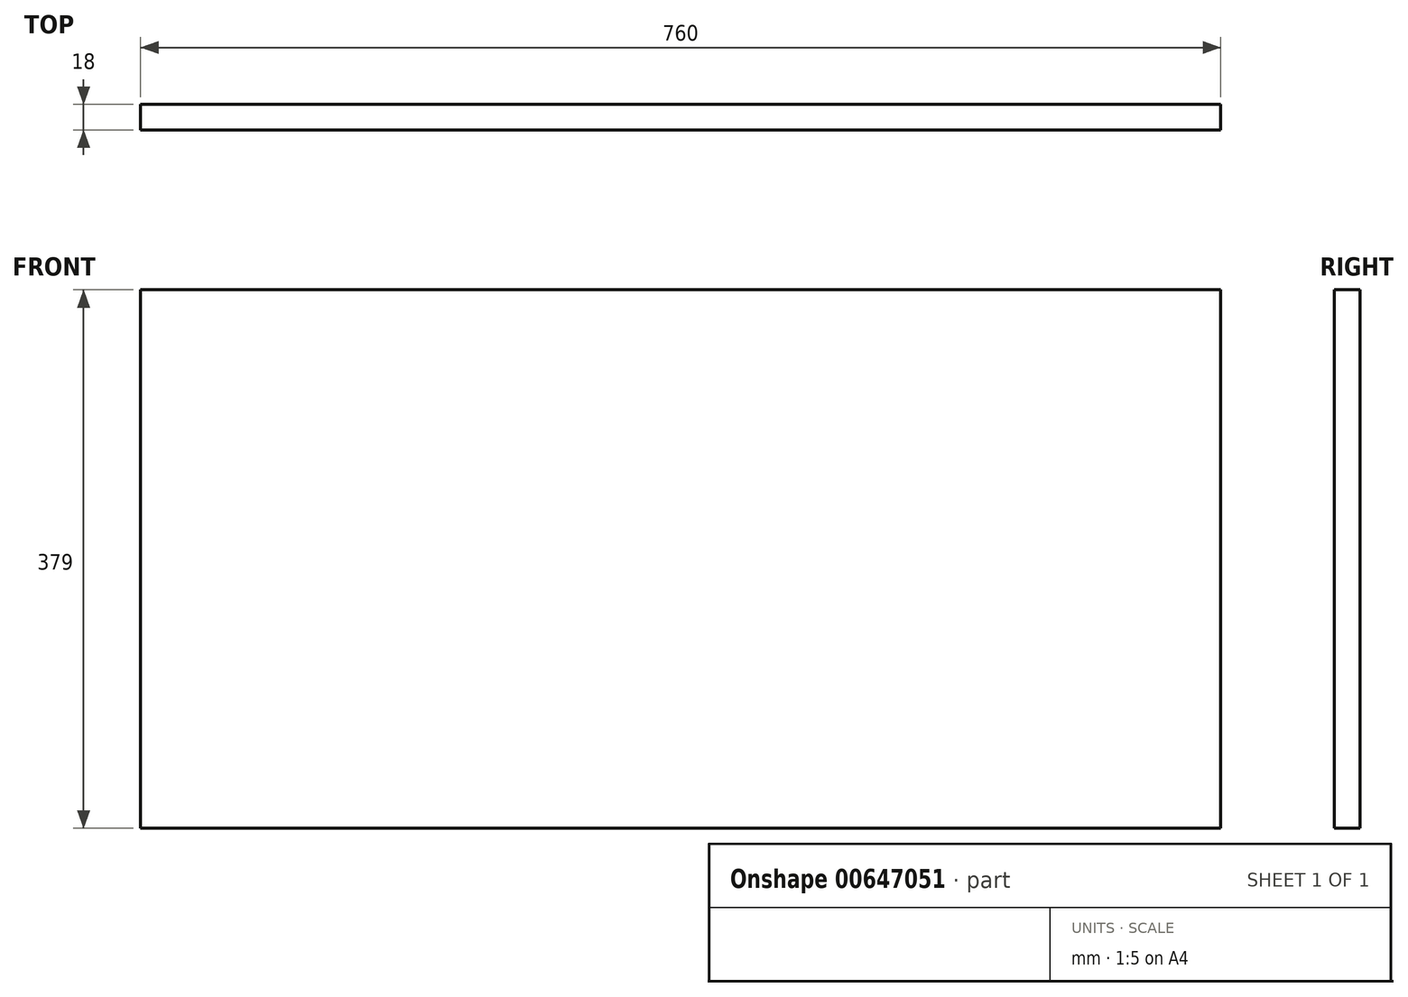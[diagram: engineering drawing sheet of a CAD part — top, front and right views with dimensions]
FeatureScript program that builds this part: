
annotation { "Feature Type Name" : "Feature", "Feature Type Description" : "" }
export const myFeature = defineFeature(function(context is Context, id is Id, definition is map)
    precondition{}
    {
        {
            var Q0;
            Q0=qCreatedBy(makeId("Front.planeOp"),FACE);
            var sketch = newSketch(context, id + "F0", { "sketchPlane" : qUnion([Q0])});
            skLineSegment(sketch, "E0.bottom", {"start": v(-380, 379) * mm, "end": v(380, 379) * mm});
            skLineSegment(sketch, "E0.top", {"start": v(-380, 0) * mm, "end": v(380, 0) * mm});
            skLineSegment(sketch, "E0.left", {"start": v(-380, 379) * mm, "end": v(-380, 0) * mm});
            skLineSegment(sketch, "E0.right", {"start": v(380, 379) * mm, "end": v(380, 0) * mm});
            skSolve(sketch);
        }
        {
            var Q0;
            Q0=makeQuery(id+"F0.imprint","IMPRINT",FACE,{"disambiguationData":[TD([[makeQuery(id+"F0.imprint","IMPRINT",EDGE,{"derivedFrom":sQuery(id+"F0.wireOp",EDGE,"E0.bottom")}),-1.0]])]});
            extrude(context, id + "F1", {"entities" : qUnion([Q0]), "depth" : 18 * mm, "offsetDistance" : 25 * mm});
        }
    });
